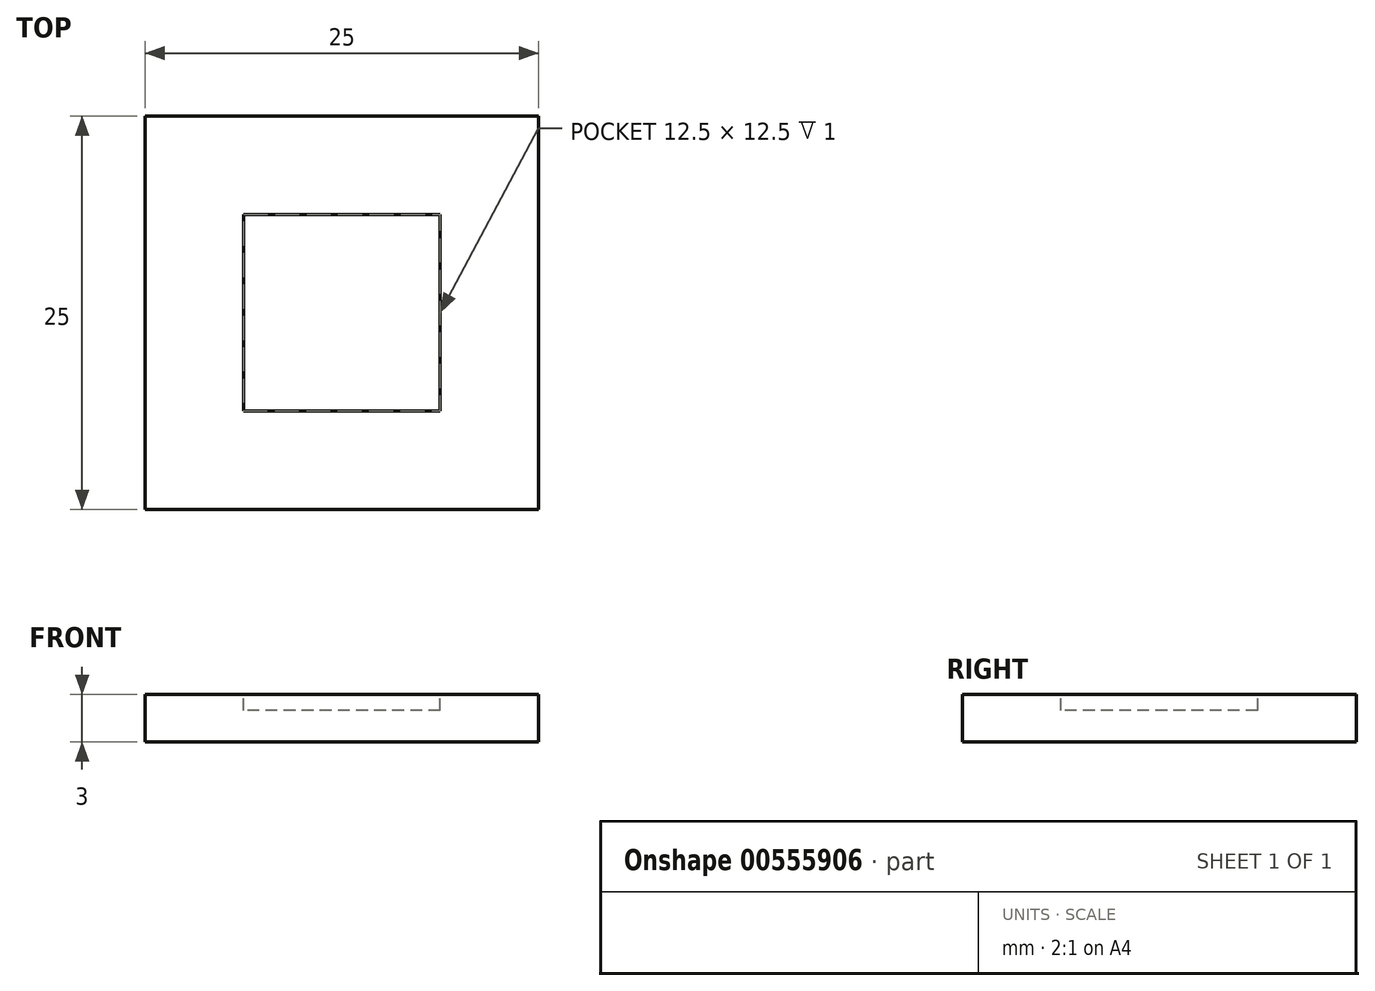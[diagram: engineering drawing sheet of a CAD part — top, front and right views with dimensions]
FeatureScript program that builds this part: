
annotation { "Feature Type Name" : "Feature", "Feature Type Description" : "" }
export const myFeature = defineFeature(function(context is Context, id is Id, definition is map)
    precondition{}
    {
        {
            var Q0;
            Q0=qCreatedBy(makeId("Top.planeOp"),FACE);
            var sketch = newSketch(context, id + "F0", { "sketchPlane" : qUnion([Q0])});
            skLineSegment(sketch, "E0.bottom", {"start": v(12.5, 12.5) * mm, "end": v(-12.5, 12.5) * mm});
            skLineSegment(sketch, "E0.top", {"start": v(12.5, -12.5) * mm, "end": v(-12.5, -12.5) * mm});
            skLineSegment(sketch, "E0.left", {"start": v(12.5, 12.5) * mm, "end": v(12.5, -12.5) * mm});
            skLineSegment(sketch, "E0.right", {"start": v(-12.5, 12.5) * mm, "end": v(-12.5, -12.5) * mm});
            skPoint(sketch, "E0.middle", {"position": v(0, 0) * mm});
            skSolve(sketch);
        }
        {
            var Q0;
            Q0 = qSketchRegion(id + "F0", true);
            extrude(context, id + "F1", {"entities" : qUnion([Q0]), "depth" : 3 * mm, "offsetDistance" : 25 * mm});
        }
        {
            var Q0;
            Q0=makeQuery(id+"F1.opExtrude","CAP_FACE",FACE,{"disambiguationData":[OSD([sQuery(id+"F0.wireOp",EDGE,"E0.bottom"),sQuery(id+"F0.wireOp",EDGE,"E0.top"),sQuery(id+"F0.wireOp",EDGE,"E0.left"),sQuery(id+"F0.wireOp",EDGE,"E0.right")])],"isStart":false});
            var sketch = newSketch(context, id + "F2", { "sketchPlane" : qUnion([Q0])});
            skLineSegment(sketch, "E1.bottom", {"start": v(6.25, 6.25) * mm, "end": v(-6.25, 6.25) * mm});
            skLineSegment(sketch, "E1.top", {"start": v(6.25, -6.25) * mm, "end": v(-6.25, -6.25) * mm});
            skLineSegment(sketch, "E1.left", {"start": v(6.25, 6.25) * mm, "end": v(6.25, -6.25) * mm});
            skLineSegment(sketch, "E1.right", {"start": v(-6.25, 6.25) * mm, "end": v(-6.25, -6.25) * mm});
            skPoint(sketch, "E1.middle", {"position": v(0, 0) * mm});
            skSolve(sketch);
        }
        {
            var Q0;
            Q0=makeQuery(id+"F2.imprint","IMPRINT",FACE,{"disambiguationData":[TD([[makeQuery(id+"F2.imprint","IMPRINT",EDGE,{"derivedFrom":sQuery(id+"F2.wireOp",EDGE,"E1.bottom")}),1.0]])]});
            extrude(context, id + "F3", {"entities" : qUnion([Q0]), "depth" : -1 * mm, "offsetDistance" : 25 * mm});
        }
        {
            var Q0;
            Q0=makeQuery(id+"F3.opExtrude","SWEPT_BODY",BODY,{"disambiguationData":[OSD([sQuery(id+"F2.wireOp",EDGE,"E1.bottom"),sQuery(id+"F2.wireOp",EDGE,"E1.top"),sQuery(id+"F2.wireOp",EDGE,"E1.left"),sQuery(id+"F2.wireOp",EDGE,"E1.right")])]});
            var Q1;
            Q1=makeQuery(id+"F1.opExtrude","SWEPT_BODY",BODY,{"disambiguationData":[OSD([sQuery(id+"F0.wireOp",EDGE,"E0.bottom"),sQuery(id+"F0.wireOp",EDGE,"E0.top"),sQuery(id+"F0.wireOp",EDGE,"E0.left"),sQuery(id+"F0.wireOp",EDGE,"E0.right")])]});
            booleanBodies(context, id + "F4", {"operationType" : BooleanOperationType.SUBTRACTION, "tools" : qUnion([Q0]), "targets" : qUnion([Q1])});
        }
    });
